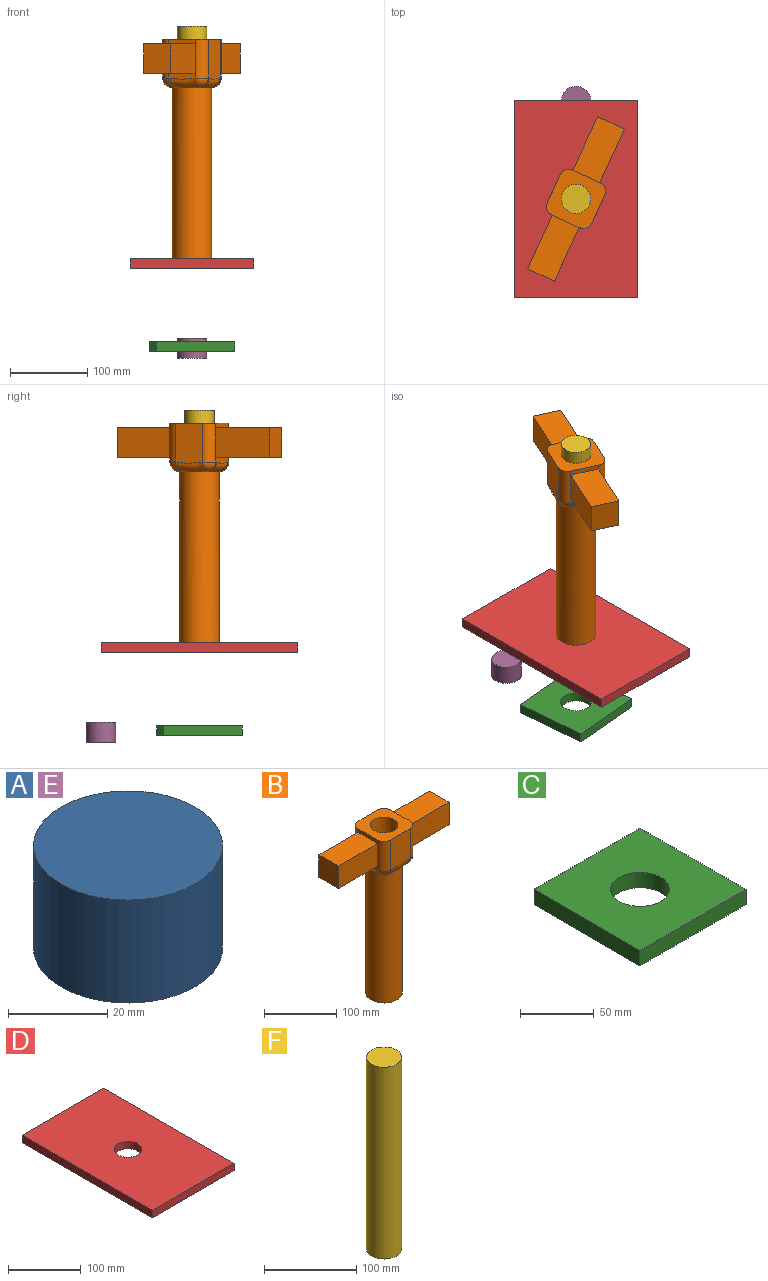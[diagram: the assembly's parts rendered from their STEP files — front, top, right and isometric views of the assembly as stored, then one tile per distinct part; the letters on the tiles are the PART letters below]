
ASSEMBLY  parts=6 mates=5
PART A: 3 faces, bbox 38.1x38.1x25.4 mm
  f0: cylinder r=19.05mm len=38.1mm, axis (0,0,-1), area 3040.2mm2, adj f1,f2
  f1: plane 38.1x38.1mm, normal (0,0,1), area 1140.1mm2, adj f0
  f2: plane 38.1x38.1mm, normal (0,0,-1), area 1140.1mm2, adj f0
PART B: 44 faces, bbox 216.3x63.5x283.5 mm
  f0: plane 38.09x6.1mm, normal (-1,0,0), area 232.2mm2, adj f12,f14,f20,f40
  f1: plane 38.09x6.1mm, normal (1,0,0), area 232.2mm2, adj f12,f23,f33,f34
  f2: plane 2.5x2.46mm, normal (0,0,-1), area 2.9mm2, adj f5,f16,f17
  f3: plane 2.5x2.46mm, normal (0,0,-1), area 2.9mm2, adj f5,f21,f26
  f4: plane 2.5x2.46mm, normal (0,0,-1), area 2.9mm2, adj f5,f30,f31
  f5: cylinder r=25.4mm len=220.47mm, axis (0,0,-1), area 35185.8mm2, adj f2,f3,f4,f7,f13,f18,f19,f28
  f6: cylinder r=19.05mm len=283.46mm, axis (0,0,-1), area 33929.1mm2, adj f7,f12
  f7: plane 50.8x50.8mm, normal (0,0,-1), area 886.7mm2, adj f5,f6
  f8: plane 38.09x7.68mm, normal (1,0,0), area 258.5mm2, adj f23,f27,f29,f31,f33,f36
  f9: plane 52x38.54mm, normal (0,1,0), area 1966.9mm2, adj f12,f20,f26,f28,f30,f33
  f10: plane 38.09x7.68mm, normal (-1,0,0), area 258.5mm2, adj f14,f16,f18,f20,f21,f42
  f11: plane 52x38.54mm, normal (0,-1,0), area 1966.9mm2, adj f12,f14,f17,f19,f22,f23
  f12: plane 63.94x63.49mm, normal (0,0,1), area 2781mm2, adj f0,f1,f6,f9,f11,f14,f20,f23
  f13: plane 2.5x2.46mm, normal (0,0,-1), area 2.9mm2, adj f5,f22,f27
  f14: cylinder r=12.7mm len=50.29mm, axis (0,0,1), area 1003.3mm2, adj f0,f10,f11,f12,f15,f39
  f15: sphere r=12.7mm, area 253.4mm2, adj f14,f16,f17
  f16: cylinder r=12.7mm len=12.7mm, axis (0,-1,0), area 49.8mm2, adj f2,f10,f15,f18
  f17: cylinder r=12.7mm len=12.7mm, axis (1,0,0), area 49.2mm2, adj f2,f11,f15,f19
  f18: bspline ~33.1x12.7mm, area 520.1mm2, adj f5,f10,f16,f21
  f19: bspline ~33.61x12.7mm, area 522.6mm2, adj f5,f11,f17,f22
  f20: cylinder r=12.7mm len=50.29mm, axis (0,0,-1), area 1003.3mm2, adj f0,f9,f10,f12,f24,f41
  f21: cylinder r=12.7mm len=12.7mm, axis (0,-1,0), area 49.8mm2, adj f3,f10,f18,f24
  f22: cylinder r=12.7mm len=12.7mm, axis (1,0,0), area 49.2mm2, adj f11,f13,f19,f25
  f23: cylinder r=12.7mm len=50.29mm, axis (0,0,-1), area 1003.3mm2, adj f1,f8,f11,f12,f25,f35
  f24: sphere r=12.7mm, area 253.4mm2, adj f20,f21,f26
  f25: sphere r=12.7mm, area 253.4mm2, adj f22,f23,f27
  f26: cylinder r=12.7mm len=12.7mm, axis (-1,0,0), area 49.2mm2, adj f3,f9,f24,f28
  f27: cylinder r=12.7mm len=12.7mm, axis (0,1,0), area 49.8mm2, adj f8,f13,f25,f29
  f28: bspline ~33.61x12.7mm, area 522.7mm2, adj f5,f9,f26,f30
  f29: bspline ~33.1x12.7mm, area 520.1mm2, adj f5,f8,f27,f31
  f30: cylinder r=12.7mm len=12.7mm, axis (-1,0,0), area 49.2mm2, adj f4,f9,f28,f32
  f31: cylinder r=12.7mm len=12.7mm, axis (0,1,0), area 49.8mm2, adj f4,f8,f29,f32
  f32: sphere r=12.7mm, area 253.4mm2, adj f30,f31,f33
  f33: cylinder r=12.7mm len=50.29mm, axis (0,0,1), area 1003.3mm2, adj f1,f8,f9,f12,f32,f37
  f34: plane 76.2x38.09mm, normal (0,0,1), area 2902.6mm2, adj f1,f35,f37,f38
  f35: plane 76.2x38.1mm, normal (0,-1,0), area 2903.2mm2, adj f23,f34,f36,f38
  f36: plane 76.2x38.09mm, normal (0,0,-1), area 2902.6mm2, adj f8,f35,f37,f38
  f37: plane 76.2x38.1mm, normal (0,1,0), area 2903.2mm2, adj f33,f34,f36,f38
  f38: plane 38.1x38.09mm, normal (1,0,0), area 1451.3mm2, adj f34,f35,f36,f37
  f39: plane 76.2x38.1mm, normal (0,-1,0), area 2903.2mm2, adj f14,f40,f42,f43
  f40: plane 76.2x38.09mm, normal (0,0,1), area 2902.6mm2, adj f0,f39,f41,f43
  f41: plane 76.2x38.1mm, normal (0,1,0), area 2903.2mm2, adj f20,f40,f42,f43
  f42: plane 76.2x38.09mm, normal (0,0,-1), area 2902.6mm2, adj f10,f39,f41,f43
  f43: plane 38.1x38.09mm, normal (-1,0,0), area 1451.3mm2, adj f39,f40,f41,f42
PART C: 7 faces, bbox 101.6x101.6x12.7 mm
  f0: plane 101.6x12.7mm, normal (1,0,0), area 1290.3mm2, adj f1,f3,f5,f6
  f1: plane 101.6x12.7mm, normal (0,1,0), area 1290.3mm2, adj f0,f2,f5,f6
  f2: plane 101.6x12.7mm, normal (-1,0,0), area 1290.3mm2, adj f1,f3,f5,f6
  f3: plane 101.6x12.7mm, normal (0,-1,0), area 1290.3mm2, adj f0,f2,f5,f6
  f4: cylinder r=19.9mm len=39.81mm, axis (0,0,-1), area 1588.2mm2, adj f5,f6
  f5: plane 101.6x101.6mm, normal (0,0,1), area 9078.1mm2, adj f0,f1,f2,f3,f4
  f6: plane 101.6x101.6mm, normal (0,0,-1), area 9078.1mm2, adj f0,f1,f2,f3,f4
PART D: 7 faces, bbox 159.3x254x12.7 mm
  f0: plane 254x12.7mm, normal (1,0,0), area 3225.8mm2, adj f1,f3,f5,f6
  f1: plane 159.32x12.7mm, normal (0,1,0), area 2023.4mm2, adj f0,f2,f5,f6
  f2: plane 254x12.7mm, normal (-1,0,0), area 3225.8mm2, adj f1,f3,f5,f6
  f3: plane 159.32x12.7mm, normal (0,-1,0), area 2023.4mm2, adj f0,f2,f5,f6
  f4: cylinder r=19.05mm len=38.1mm, axis (0,0,-1), area 1520.1mm2, adj f5,f6
  f5: plane 254x159.32mm, normal (0,0,1), area 39328.1mm2, adj f0,f1,f2,f3,f4
  f6: plane 254x159.32mm, normal (0,0,-1), area 39328.1mm2, adj f0,f1,f2,f3,f4
PART E: same geometry as A
PART F: 3 faces, bbox 38.1x38.1x254 mm
  f0: cylinder r=19.05mm len=254mm, axis (0,0,-1), area 30402.4mm2, adj f1,f2
  f1: plane 38.1x38.1mm, normal (0,0,1), area 1140.1mm2, adj f0
  f2: plane 38.1x38.1mm, normal (0,0,-1), area 1140.1mm2, adj f0
PLACE A rot(axis=(0,0,-1),84.9deg) t=(-182.68,-153.17,-31.49)mm
PLACE B rot(axis=(0,0,1),65.3deg) t=(-182.68,-153.17,61.8)mm
PLACE C rot(axis=(0,0,1),95.1deg) t=(-182.68,-153.17,-185.33)mm fixed
PLACE D t=(-182.68,-153.17,-77.9)mm fixed
PLACE E rot(axis=(0,1,0),180deg) t=(-182.68,-26.17,-180.94)mm
PLACE F rot(axis=(0,0,-1),174.9deg) t=(-182.68,-153.17,108.21)mm
MATE revolute B.f6 <-> D.f4  axis (0,0,-1) through (-182.68,-153.17,-65.2)mm
MATE slider C.f4 <-> A.f0  axis (0,0,-1) through (-182.68,-153.17,-172.63)mm
MATE fastened A.f0 <-> F.f0  axis (0,0,-1) through (-182.68,-153.17,-18.79)mm
MATE slider D.f5 <-> E.f0  axis (0,0,1) through (-182.68,-26.17,-65.2)mm
MATE cylindrical F.f0 <-> B.f6  axis (0,0,-1) through (-182.68,-153.17,235.21)mm
